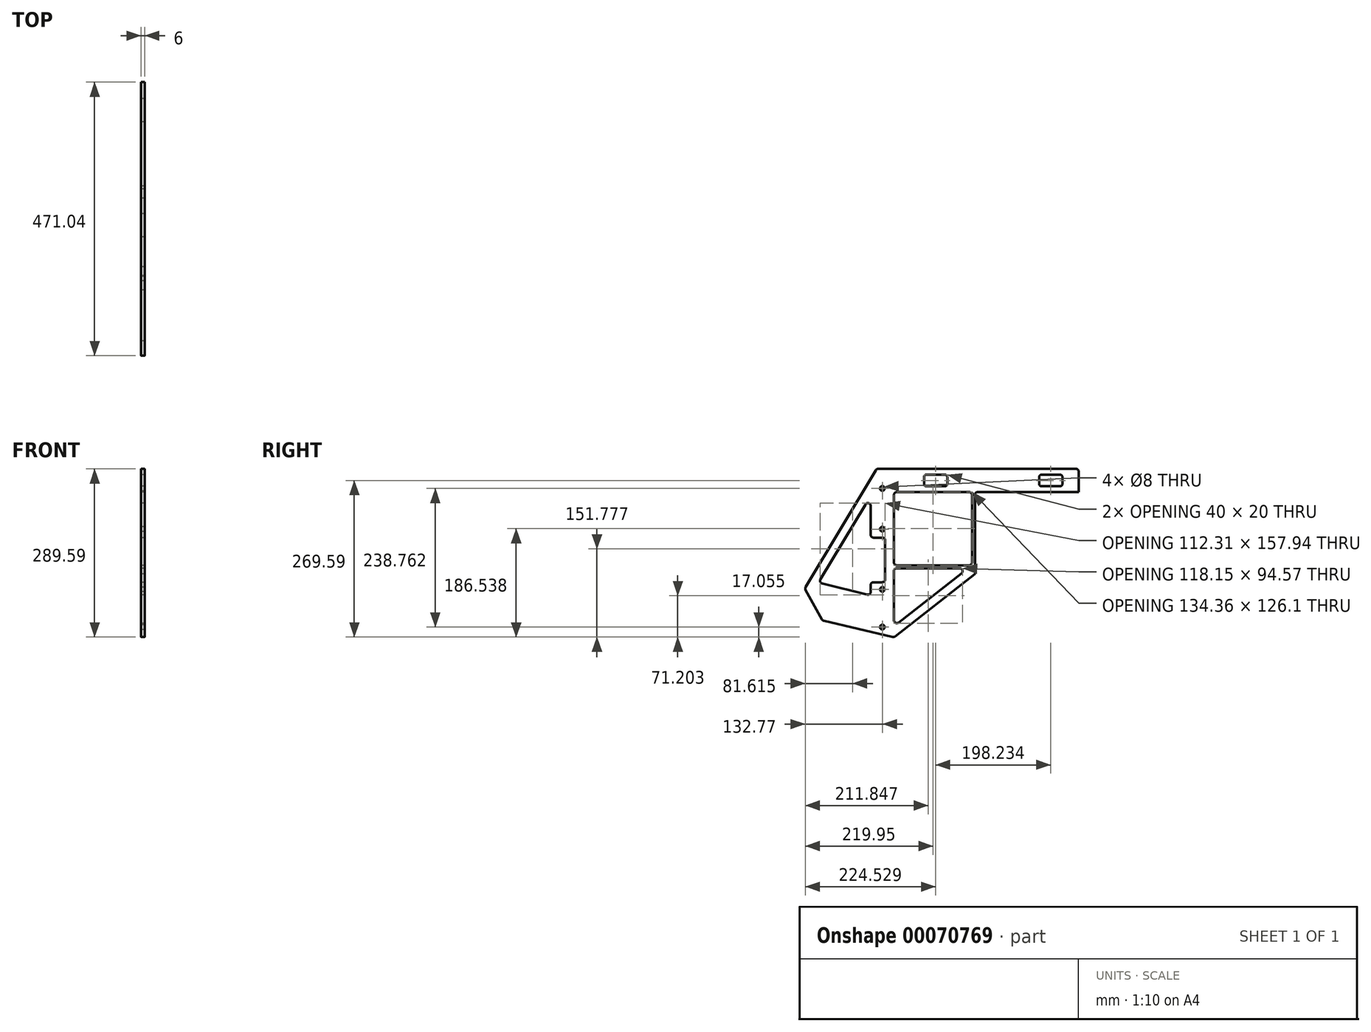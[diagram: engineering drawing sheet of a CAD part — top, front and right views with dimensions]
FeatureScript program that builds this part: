
annotation { "Feature Type Name" : "Feature", "Feature Type Description" : "" }
export const myFeature = defineFeature(function(context is Context, id is Id, definition is map)
    precondition{}
    {
        {
            var Q0;
            Q0=qCreatedBy(makeId("Right.planeOp"),FACE);
            var sketch = newSketch(context, id + "F0", { "sketchPlane" : qUnion([Q0])});
            skLineSegment(sketch, "E0.bottom", {"start": v(35, 0) * mm, "end": v(159.36, 0) * mm});
            skLineSegment(sketch, "E0.top", {"start": v(2.83, 40) * mm, "end": v(343.27, 40) * mm});
            skLineSegment(sketch, "E1", {"start": v(30, -5) * mm, "end": v(30, -121.1) * mm});
            skLineSegment(sketch, "E2", {"start": v(-1.46, 37.57) * mm, "end": v(-122.06, -163.3) * mm});
            skLineSegment(sketch, "E3", {"start": v(-122.15, -168.28) * mm, "end": v(-94, -219.32) * mm});
            skLineSegment(sketch, "E4", {"start": v(-90.76, -221.77) * mm, "end": v(27.67, -249.45) * mm});
            skLineSegment(sketch, "E5", {"start": v(169.36, -141) * mm, "end": v(31.89, -248.52) * mm});
            skPoint(sketch, "E6.visualSharp", {"position": v(325.28, 0) * mm});
            skArc(sketch, "E6.filletArc", {"start": v(313.85, -8.94) * mm, "mid": v(315.5, -3.37) * mm, "end": v(310.77, 0) * mm});
            skPoint(sketch, "E7.visualSharp", {"position": v(30, -230.96) * mm});
            skArc(sketch, "E7.filletArc", {"start": v(30, -220.7) * mm, "mid": v(32.8, -225.2) * mm, "end": v(38.08, -224.64) * mm});
            skPoint(sketch, "E8.visualSharp", {"position": v(30, -250) * mm});
            skArc(sketch, "E8.filletArc", {"start": v(27.67, -249.45) * mm, "mid": v(29.88, -249.47) * mm, "end": v(31.89, -248.52) * mm});
            skPoint(sketch, "E9.visualSharp", {"position": v(30, 0) * mm});
            skArc(sketch, "E9.filletArc", {"start": v(35, 0) * mm, "mid": v(31.46, -1.46) * mm, "end": v(30, -5) * mm});
            skPoint(sketch, "E10.visualSharp", {"position": v(0, 40) * mm});
            skArc(sketch, "E10.filletArc", {"start": v(2.83, 40) * mm, "mid": v(0.37, 39.35) * mm, "end": v(-1.46, 37.57) * mm});
            skPoint(sketch, "E11.visualSharp", {"position": v(-123.54, -165.76) * mm});
            skArc(sketch, "E11.filletArc", {"start": v(-122.06, -163.3) * mm, "mid": v(-122.77, -165.77) * mm, "end": v(-122.15, -168.28) * mm});
            skPoint(sketch, "E12.visualSharp", {"position": v(-92.93, -221.27) * mm});
            skArc(sketch, "E12.filletArc", {"start": v(-94, -219.32) * mm, "mid": v(-92.64, -220.89) * mm, "end": v(-90.76, -221.77) * mm});
            skLineSegment(sketch, "E13.trimOffspring", {"start": v(-19.29, -21.26) * mm, "end": v(-96.6, -150.04) * mm});
            skLineSegment(sketch, "E14.trimOffspring", {"start": v(15, -83.43) * mm, "end": v(15, -150.19) * mm});
            skLineSegment(sketch, "E15", {"start": v(-93.53, -157.47) * mm, "end": v(-16.2, -176.64) * mm});
            skPoint(sketch, "E16.visualSharp", {"position": v(-100.1, -155.84) * mm});
            skArc(sketch, "E16.filletArc", {"start": v(-96.6, -150.04) * mm, "mid": v(-96.94, -154.54) * mm, "end": v(-93.53, -157.47) * mm});
            skLineSegment(sketch, "E17", {"start": v(164.36, -5) * mm, "end": v(164.36, -107.12) * mm});
            skLineSegment(sketch, "E18", {"start": v(35, -131.1) * mm, "end": v(143.15, -131.1) * mm});
            skLineSegment(sketch, "E19", {"start": v(35, -126.1) * mm, "end": v(151.24, -126.1) * mm});
            skLineSegment(sketch, "E20", {"start": v(169.36, -5) * mm, "end": v(169.36, -95.98) * mm});
            skLineSegment(sketch, "E21.trimOffspring", {"start": v(30, -136.1) * mm, "end": v(30, -220.7) * mm});
            skLineSegment(sketch, "E22.trimOffspring", {"start": v(146.24, -140.04) * mm, "end": v(38.08, -224.64) * mm});
            skPoint(sketch, "E23.visualSharp", {"position": v(157.66, -131.1) * mm});
            skArc(sketch, "E23.filletArc", {"start": v(146.24, -140.04) * mm, "mid": v(147.88, -134.48) * mm, "end": v(143.15, -131.1) * mm});
            skPoint(sketch, "E24.visualSharp", {"position": v(164.36, -126.1) * mm});
            skPoint(sketch, "E25.visualSharp", {"position": v(169.36, -121.95) * mm});
            skLineSegment(sketch, "E26", {"start": v(151.24, -126.1) * mm, "end": v(159.36, -126.1) * mm});
            skLineSegment(sketch, "E27", {"start": v(164.36, -107.12) * mm, "end": v(164.36, -121.1) * mm});
            skArc(sketch, "E28.filletArc", {"start": v(159.36, -126.1) * mm, "mid": v(162.9, -124.64) * mm, "end": v(164.36, -121.1) * mm});
            skLineSegment(sketch, "E29", {"start": v(169.36, -95.98) * mm, "end": v(169.36, -111.7) * mm});
            skLineSegment(sketch, "E30", {"start": v(183.61, -110.8) * mm, "end": v(177.44, -115.63) * mm});
            skArc(sketch, "E31.filletArc", {"start": v(169.36, -111.7) * mm, "mid": v(172.17, -116.2) * mm, "end": v(177.44, -115.63) * mm});
            skLineSegment(sketch, "E32.trimOffspring", {"start": v(174.36, 0) * mm, "end": v(310.77, 0) * mm});
            skArc(sketch, "E33.filletArc", {"start": v(174.36, 0) * mm, "mid": v(170.83, -1.46) * mm, "end": v(169.36, -5) * mm});
            skArc(sketch, "E34.filletArc", {"start": v(164.36, -5) * mm, "mid": v(162.9, -1.46) * mm, "end": v(159.36, 0) * mm});
            skPoint(sketch, "E35.visualSharp", {"position": v(30, -126.1) * mm});
            skArc(sketch, "E35.filletArc", {"start": v(30, -121.1) * mm, "mid": v(31.46, -124.64) * mm, "end": v(35, -126.1) * mm});
            skPoint(sketch, "E36.visualSharp", {"position": v(30, -131.1) * mm});
            skArc(sketch, "E36.filletArc", {"start": v(35, -131.1) * mm, "mid": v(31.46, -132.57) * mm, "end": v(30, -136.1) * mm});
            skLineSegment(sketch, "E37", {"start": v(284, 30) * mm, "end": v(316, 30) * mm});
            skLineSegment(sketch, "E38", {"start": v(320, 26) * mm, "end": v(320, 20) * mm});
            skLineSegment(sketch, "E39", {"start": v(280, 26) * mm, "end": v(280, 20) * mm});
            skPoint(sketch, "E40.visualSharp", {"position": v(280, 30) * mm});
            skArc(sketch, "E40.filletArc", {"start": v(284, 30) * mm, "mid": v(281.16, 28.83) * mm, "end": v(280, 26) * mm});
            skPoint(sketch, "E41.visualSharp", {"position": v(320, 30) * mm});
            skArc(sketch, "E41.filletArc", {"start": v(320, 26) * mm, "mid": v(318.82, 28.83) * mm, "end": v(316, 30) * mm});
            skLineSegment(sketch, "E42.MirrorCS", {"start": v(284, 10) * mm, "end": v(316, 10) * mm});
            skPoint(sketch, "E43.MirrorP", {"position": v(280, 10) * mm});
            skArc(sketch, "E44.MirrorCS", {"start": v(320, 14) * mm, "mid": v(318.82, 11.17) * mm, "end": v(316, 10) * mm});
            skPoint(sketch, "E45.MirrorP", {"position": v(320, 10) * mm});
            skArc(sketch, "E46.MirrorCS", {"start": v(284, 10) * mm, "mid": v(281.16, 11.17) * mm, "end": v(280, 14) * mm});
            skLineSegment(sketch, "E47.MirrorCS", {"start": v(280, 14) * mm, "end": v(280, 20) * mm});
            skLineSegment(sketch, "E48.MirrorCS", {"start": v(320, 14) * mm, "end": v(320, 20) * mm});
            skLineSegment(sketch, "E49", {"start": v(200.88, 50.97) * mm, "end": v(200.88, -9.9) * mm, "construction": true});
            skArc(sketch, "E50.MirrorCS", {"start": v(117.76, 10) * mm, "mid": v(120.59, 11.17) * mm, "end": v(121.76, 14) * mm});
            skArc(sketch, "E51.MirrorCS", {"start": v(81.76, 14) * mm, "mid": v(82.93, 11.17) * mm, "end": v(85.76, 10) * mm});
            skArc(sketch, "E52.MirrorCS", {"start": v(81.76, 26) * mm, "mid": v(82.93, 28.83) * mm, "end": v(85.76, 30) * mm});
            skArc(sketch, "E53.MirrorCS", {"start": v(117.76, 30) * mm, "mid": v(120.59, 28.83) * mm, "end": v(121.76, 26) * mm});
            skLineSegment(sketch, "E54.MirrorCS", {"start": v(81.76, 14) * mm, "end": v(81.76, 20) * mm});
            skLineSegment(sketch, "E55.MirrorCS", {"start": v(121.76, 14) * mm, "end": v(121.76, 20) * mm});
            skPoint(sketch, "E56.MirrorP", {"position": v(81.76, 30) * mm});
            skPoint(sketch, "E57.MirrorP", {"position": v(121.76, 30) * mm});
            skPoint(sketch, "E58.MirrorP", {"position": v(121.76, 10) * mm});
            skPoint(sketch, "E59.MirrorP", {"position": v(81.76, 10) * mm});
            skLineSegment(sketch, "E60.MirrorCS", {"start": v(81.76, 26) * mm, "end": v(81.76, 20) * mm});
            skLineSegment(sketch, "E61.MirrorCS", {"start": v(117.76, 10) * mm, "end": v(85.76, 10) * mm});
            skLineSegment(sketch, "E62.MirrorCS", {"start": v(121.76, 26) * mm, "end": v(121.76, 20) * mm});
            skLineSegment(sketch, "E63.MirrorCS", {"start": v(117.76, 30) * mm, "end": v(85.76, 30) * mm});
            skLineSegment(sketch, "E64.trimOffspring", {"start": v(-10, -23.84) * mm, "end": v(-10, -73.43) * mm});
            skLineSegment(sketch, "E65", {"start": v(-5, -155.19) * mm, "end": v(10, -155.19) * mm});
            skPoint(sketch, "E66.visualSharp", {"position": v(15, -155.19) * mm});
            skArc(sketch, "E66.filletArc", {"start": v(10, -155.19) * mm, "mid": v(13.54, -153.72) * mm, "end": v(15, -150.19) * mm});
            skPoint(sketch, "E67.visualSharp", {"position": v(-10, -178.17) * mm});
            skArc(sketch, "E67.filletArc", {"start": v(-16.2, -176.64) * mm, "mid": v(-11.92, -175.72) * mm, "end": v(-10, -171.78) * mm});
            skLineSegment(sketch, "E68", {"start": v(-5, -78.43) * mm, "end": v(10, -78.43) * mm});
            skLineSegment(sketch, "E69.trimOffspring", {"start": v(-10, -160.19) * mm, "end": v(-10, -171.78) * mm});
            skPoint(sketch, "E70.visualSharp", {"position": v(-10, -155.19) * mm});
            skArc(sketch, "E70.filletArc", {"start": v(-5, -155.19) * mm, "mid": v(-8.54, -156.65) * mm, "end": v(-10, -160.19) * mm});
            skArc(sketch, "E71.filletArc", {"start": v(15, -83.43) * mm, "mid": v(13.54, -79.9) * mm, "end": v(10, -78.43) * mm});
            skPoint(sketch, "E72.visualSharp", {"position": v(-10, -78.43) * mm});
            skArc(sketch, "E72.filletArc", {"start": v(-10, -73.43) * mm, "mid": v(-8.54, -76.96) * mm, "end": v(-5, -78.43) * mm});
            skArc(sketch, "E73.filletArc", {"start": v(-10, -23.84) * mm, "mid": v(-13.66, -19.02) * mm, "end": v(-19.29, -21.26) * mm});
            skLineSegment(sketch, "E74", {"start": v(10, 51.17) * mm, "end": v(10, -264.25) * mm, "construction": true});
            skCircle(sketch, "E75", {"center": v(10, -63.77) * mm, "radius": 4 * mm});
            skCircle(sketch, "E76", {"center": v(10, 6.23) * mm, "radius": 4 * mm});
            skCircle(sketch, "E77", {"center": v(10, -232.53) * mm, "radius": 4 * mm});
            skCircle(sketch, "E78", {"center": v(10, -167.53) * mm, "radius": 4 * mm});
            skLineSegment(sketch, "E79", {"start": v(348.27, 1.38) * mm, "end": v(348.27, 35) * mm});
            skArc(sketch, "E80.filletArc", {"start": v(348.27, 35) * mm, "mid": v(346.8, 38.54) * mm, "end": v(343.27, 40) * mm});
            skPoint(sketch, "E81.visualSharp", {"position": v(348.27, -1.06) * mm});
            skArc(sketch, "E81.filletArc", {"start": v(346.35, -2.56) * mm, "mid": v(347.77, -0.82) * mm, "end": v(348.27, 1.38) * mm});
            skLineSegment(sketch, "E82", {"start": v(310.77, 0) * mm, "end": v(348.08, 0) * mm});
            skLineSegment(sketch, "E83", {"start": v(169.36, -111.7) * mm, "end": v(169.36, -141) * mm});
            skSolve(sketch);
        }
        {
            var Q0;
            Q0=makeQuery(id+"F0.imprint","IMPRINT",FACE,{"disambiguationData":[TD([[makeQuery(id+"F0.imprint","IMPRINT",EDGE,{"derivedFrom":sQuery(id+"F0.wireOp",EDGE,"E0.bottom")}),1.0]])]});
            extrude(context, id + "F1", {"entities" : qUnion([Q0]), "depth" : 6 * mm, "offsetDistance" : 25 * mm});
        }
    });
